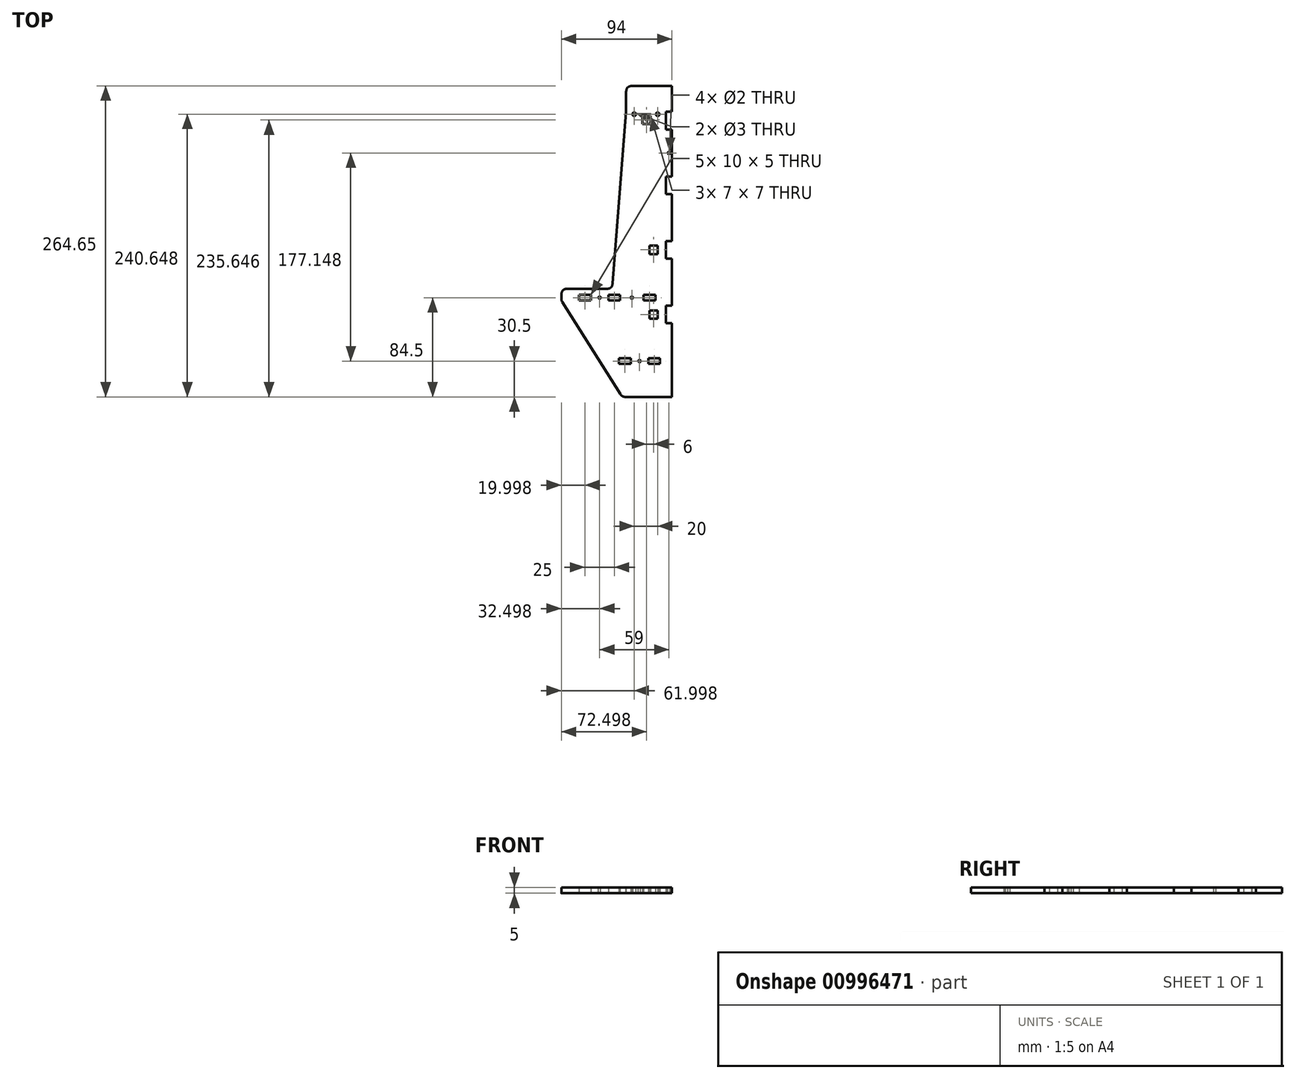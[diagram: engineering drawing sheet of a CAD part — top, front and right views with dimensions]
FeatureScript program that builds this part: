
annotation { "Feature Type Name" : "Feature", "Feature Type Description" : "" }
export const myFeature = defineFeature(function(context is Context, id is Id, definition is map)
    precondition{}
    {
        {
            var Q0;
            Q0=qCreatedBy(makeId("Top.planeOp"),FACE);
            var sketch = newSketch(context, id + "F0", { "sketchPlane" : qUnion([Q0])});
            skLineSegment(sketch, "E0", {"start": v(-76.42, -54.81) * mm, "end": v(-76.42, -44.81) * mm});
            skLineSegment(sketch, "E1", {"start": v(-33.23, -44.81) * mm, "end": v(-21.3, 105.84) * mm});
            skLineSegment(sketch, "E2", {"start": v(-21.3, 105.84) * mm, "end": v(12.58, 105.84) * mm, "construction": true});
            skLineSegment(sketch, "E3", {"start": v(17.58, 90.84) * mm, "end": v(17.58, 50.84) * mm});
            skLineSegment(sketch, "E4", {"start": v(17.58, -136.81) * mm, "end": v(-24.72, -136.81) * mm});
            skLineSegment(sketch, "E5", {"start": v(-24.72, -136.81) * mm, "end": v(-76.42, -54.81) * mm});
            skLineSegment(sketch, "E6.bottom", {"start": v(17.58, -74.16) * mm, "end": v(12.58, -74.16) * mm});
            skLineSegment(sketch, "E6.top", {"start": v(17.58, -59.16) * mm, "end": v(12.58, -59.16) * mm});
            skLineSegment(sketch, "E6.right", {"start": v(12.58, -74.16) * mm, "end": v(12.58, -59.16) * mm});
            skLineSegment(sketch, "E7.bottom", {"start": v(17.58, -19.16) * mm, "end": v(12.58, -19.16) * mm});
            skLineSegment(sketch, "E7.top", {"start": v(17.58, -4.16) * mm, "end": v(12.58, -4.16) * mm});
            skLineSegment(sketch, "E7.right", {"start": v(12.58, -19.16) * mm, "end": v(12.58, -4.16) * mm});
            skLineSegment(sketch, "E8.bottom", {"start": v(17.58, 35.84) * mm, "end": v(12.58, 35.84) * mm});
            skLineSegment(sketch, "E8.top", {"start": v(17.58, 50.84) * mm, "end": v(12.58, 50.84) * mm});
            skLineSegment(sketch, "E8.right", {"start": v(12.58, 35.84) * mm, "end": v(12.58, 50.84) * mm});
            skLineSegment(sketch, "E9.bottom", {"start": v(17.58, 90.84) * mm, "end": v(12.58, 90.84) * mm});
            skLineSegment(sketch, "E9.right", {"start": v(12.58, 90.84) * mm, "end": v(12.58, 105.84) * mm});
            skLineSegment(sketch, "E10.trimOffspring", {"start": v(17.58, 35.84) * mm, "end": v(17.58, -4.16) * mm});
            skLineSegment(sketch, "E11.trimOffspring", {"start": v(17.58, -19.16) * mm, "end": v(17.58, -59.16) * mm});
            skLineSegment(sketch, "E12.trimOffspring", {"start": v(17.58, -74.16) * mm, "end": v(17.58, -136.81) * mm});
            skPoint(sketch, "E13", {"position": v(17.58, -108.81) * mm});
            skLineSegment(sketch, "E14", {"start": v(17.58, -108.81) * mm, "end": v(-42.38, -108.81) * mm, "construction": true});
            skLineSegment(sketch, "E15.bottom", {"start": v(-2.42, -108.81) * mm, "end": v(7.58, -108.81) * mm});
            skLineSegment(sketch, "E15.top", {"start": v(-2.42, -103.81) * mm, "end": v(7.58, -103.81) * mm});
            skLineSegment(sketch, "E15.left", {"start": v(-2.42, -108.81) * mm, "end": v(-2.42, -103.81) * mm});
            skLineSegment(sketch, "E15.right", {"start": v(7.58, -108.81) * mm, "end": v(7.58, -103.81) * mm});
            skLineSegment(sketch, "E16.bottom", {"start": v(-27.42, -108.81) * mm, "end": v(-17.42, -108.81) * mm});
            skLineSegment(sketch, "E16.top", {"start": v(-27.42, -103.81) * mm, "end": v(-17.42, -103.81) * mm});
            skLineSegment(sketch, "E16.left", {"start": v(-27.42, -108.81) * mm, "end": v(-27.42, -103.81) * mm});
            skLineSegment(sketch, "E16.right", {"start": v(-17.42, -108.81) * mm, "end": v(-17.42, -103.81) * mm});
            skLineSegment(sketch, "E17", {"start": v(-76.42, -54.81) * mm, "end": v(17.58, -54.81) * mm, "construction": true});
            skLineSegment(sketch, "E18.bottom", {"start": v(-61.42, -54.81) * mm, "end": v(-51.42, -54.81) * mm});
            skLineSegment(sketch, "E18.top", {"start": v(-61.42, -49.81) * mm, "end": v(-51.42, -49.81) * mm});
            skLineSegment(sketch, "E18.left", {"start": v(-61.42, -54.81) * mm, "end": v(-61.42, -49.81) * mm});
            skLineSegment(sketch, "E18.right", {"start": v(-51.42, -54.81) * mm, "end": v(-51.42, -49.81) * mm});
            skLineSegment(sketch, "E19.bottom", {"start": v(-36.42, -54.81) * mm, "end": v(-26.42, -54.81) * mm});
            skLineSegment(sketch, "E19.top", {"start": v(-36.42, -49.81) * mm, "end": v(-26.42, -49.81) * mm});
            skLineSegment(sketch, "E19.left", {"start": v(-36.42, -54.81) * mm, "end": v(-36.42, -49.81) * mm});
            skLineSegment(sketch, "E19.right", {"start": v(-26.42, -54.81) * mm, "end": v(-26.42, -49.81) * mm});
            skLineSegment(sketch, "E20.bottom", {"start": v(-6.42, -54.81) * mm, "end": v(3.58, -54.81) * mm});
            skLineSegment(sketch, "E20.top", {"start": v(-6.42, -49.81) * mm, "end": v(3.58, -49.81) * mm});
            skLineSegment(sketch, "E20.left", {"start": v(-6.42, -54.81) * mm, "end": v(-6.42, -49.81) * mm});
            skLineSegment(sketch, "E20.right", {"start": v(3.58, -54.81) * mm, "end": v(3.58, -49.81) * mm});
            skPoint(sketch, "E21", {"position": v(-76.42, -44.81) * mm});
            skLineSegment(sketch, "E22", {"start": v(-33.23, -44.81) * mm, "end": v(17.58, -44.81) * mm, "construction": true});
            skLineSegment(sketch, "E23", {"start": v(-76.42, -44.81) * mm, "end": v(-33.23, -44.81) * mm});
            skLineSegment(sketch, "E24", {"start": v(-21.3, 105.84) * mm, "end": v(-21.3, 127.84) * mm});
            skLineSegment(sketch, "E25", {"start": v(-21.3, 127.84) * mm, "end": v(17.58, 127.84) * mm});
            skLineSegment(sketch, "E26", {"start": v(17.58, 127.84) * mm, "end": v(17.58, 105.84) * mm});
            skLineSegment(sketch, "E27", {"start": v(17.58, 105.84) * mm, "end": v(12.58, 105.84) * mm});
            skLineSegment(sketch, "E28.bottom", {"start": v(-7.42, 102.34) * mm, "end": v(-0.42, 102.34) * mm});
            skLineSegment(sketch, "E28.top", {"start": v(-7.42, 95.34) * mm, "end": v(-0.42, 95.34) * mm});
            skLineSegment(sketch, "E28.left", {"start": v(-7.42, 102.34) * mm, "end": v(-7.42, 95.34) * mm});
            skLineSegment(sketch, "E28.right", {"start": v(-0.42, 102.34) * mm, "end": v(-0.42, 95.34) * mm});
            skLineSegment(sketch, "E29.bottom", {"start": v(-1.42, -8.16) * mm, "end": v(5.58, -8.16) * mm});
            skLineSegment(sketch, "E29.top", {"start": v(-1.42, -15.16) * mm, "end": v(5.58, -15.16) * mm});
            skLineSegment(sketch, "E29.left", {"start": v(-1.42, -8.16) * mm, "end": v(-1.42, -15.16) * mm});
            skLineSegment(sketch, "E29.right", {"start": v(5.58, -8.16) * mm, "end": v(5.58, -15.16) * mm});
            skLineSegment(sketch, "E30.bottom", {"start": v(-1.42, -63.16) * mm, "end": v(5.58, -63.16) * mm});
            skLineSegment(sketch, "E30.top", {"start": v(-1.42, -70.16) * mm, "end": v(5.58, -70.16) * mm});
            skLineSegment(sketch, "E30.left", {"start": v(-1.42, -63.16) * mm, "end": v(-1.42, -70.16) * mm});
            skLineSegment(sketch, "E30.right", {"start": v(5.58, -63.16) * mm, "end": v(5.58, -70.16) * mm});
            skPoint(sketch, "E31", {"position": v(5.58, -11.66) * mm});
            skPoint(sketch, "E32", {"position": v(12.58, -11.66) * mm});
            skPoint(sketch, "E33", {"position": v(5.58, -66.66) * mm});
            skPoint(sketch, "E34", {"position": v(12.58, -66.66) * mm});
            skSolve(sketch);
        }
        {
            var Q0;
            Q0=makeQuery(id+"F0.imprint","IMPRINT",FACE,{"disambiguationData":[TD([[makeQuery(id+"F0.imprint","IMPRINT",EDGE,{"derivedFrom":sQuery(id+"F0.wireOp",EDGE,"E0")}),-1.0]])]});
            extrude(context, id + "F1", {"entities" : qUnion([Q0]), "depth" : 5 * mm, "offsetDistance" : 25 * mm});
        }
        {
            var Q0;
            Q0=makeQuery(id+"F1.opExtrude","SWEPT_EDGE",EDGE,{"disambiguationData":[OSD([sQuery(id+"F0.wireOp",EDGE,"E4"),sQuery(id+"F0.wireOp",EDGE,"E5")])]});
            var Q1;
            Q1=makeQuery(id+"F1.opExtrude","SWEPT_EDGE",EDGE,{"disambiguationData":[OSD([sQuery(id+"F0.wireOp",EDGE,"E4"),sQuery(id+"F0.wireOp",EDGE,"E5")])]});
            var Q2;
            Q2=makeQuery(id+"F1.opExtrude","SWEPT_EDGE",EDGE,{"disambiguationData":[OSD([sQuery(id+"F0.wireOp",EDGE,"E1"),sQuery(id+"F0.wireOp",EDGE,"E23")])]});
            var Q3;
            Q3=makeQuery(id+"F1.opExtrude","SWEPT_EDGE",EDGE,{"disambiguationData":[OSD([sQuery(id+"F0.wireOp",EDGE,"E0"),sQuery(id+"F0.wireOp",EDGE,"E5")])]});
            var Q4;
            Q4=makeQuery(id+"F1.opExtrude","SWEPT_EDGE",EDGE,{"disambiguationData":[OSD([sQuery(id+"F0.wireOp",EDGE,"E0"),sQuery(id+"F0.wireOp",EDGE,"E23")])]});
            var Q5;
            Q5=makeQuery(id+"F1.opExtrude","SWEPT_EDGE",EDGE,{"disambiguationData":[OSD([sQuery(id+"F0.wireOp",EDGE,"E1"),sQuery(id+"F0.wireOp",EDGE,"E24")])]});
            var Q6;
            Q6=makeQuery(id+"F1.opExtrude","SWEPT_EDGE",EDGE,{"disambiguationData":[OSD([sQuery(id+"F0.wireOp",EDGE,"E24"),sQuery(id+"F0.wireOp",EDGE,"E25")])]});
            fillet(context, id + "F2", {"entities" : qUnion([Q0, Q1, Q2, Q3, Q4, Q5, Q6]), "radius" : 5 * mm, "tangentPropagation" : true, "rho" : 0.5, "crossSection" : FilletCrossSection.CONIC, "allowEdgeOverflow" : false});
        }
        {
            var Q0;
            Q0=makeQuery(id+"F1.opExtrude","CAP_FACE",FACE,{"disambiguationData":[OSD([sQuery(id+"F0.wireOp",EDGE,"E0"),sQuery(id+"F0.wireOp",EDGE,"E1"),sQuery(id+"F0.wireOp",EDGE,"E3"),sQuery(id+"F0.wireOp",EDGE,"E4"),sQuery(id+"F0.wireOp",EDGE,"E5"),sQuery(id+"F0.wireOp",EDGE,"E6.bottom"),sQuery(id+"F0.wireOp",EDGE,"E6.top"),sQuery(id+"F0.wireOp",EDGE,"E6.right"),sQuery(id+"F0.wireOp",EDGE,"E7.bottom"),sQuery(id+"F0.wireOp",EDGE,"E7.top"),sQuery(id+"F0.wireOp",EDGE,"E7.right"),sQuery(id+"F0.wireOp",EDGE,"E8.bottom"),sQuery(id+"F0.wireOp",EDGE,"E8.top"),sQuery(id+"F0.wireOp",EDGE,"E8.right"),sQuery(id+"F0.wireOp",EDGE,"E9.bottom"),sQuery(id+"F0.wireOp",EDGE,"E9.right"),sQuery(id+"F0.wireOp",EDGE,"E10.trimOffspring"),sQuery(id+"F0.wireOp",EDGE,"E11.trimOffspring"),sQuery(id+"F0.wireOp",EDGE,"E12.trimOffspring"),sQuery(id+"F0.wireOp",EDGE,"E15.bottom"),sQuery(id+"F0.wireOp",EDGE,"E15.top"),sQuery(id+"F0.wireOp",EDGE,"E15.left"),sQuery(id+"F0.wireOp",EDGE,"E15.right"),sQuery(id+"F0.wireOp",EDGE,"E16.bottom"),sQuery(id+"F0.wireOp",EDGE,"E16.top"),sQuery(id+"F0.wireOp",EDGE,"E16.left"),sQuery(id+"F0.wireOp",EDGE,"E16.right"),sQuery(id+"F0.wireOp",EDGE,"E18.bottom"),sQuery(id+"F0.wireOp",EDGE,"E18.top"),sQuery(id+"F0.wireOp",EDGE,"E18.left"),sQuery(id+"F0.wireOp",EDGE,"E18.right"),sQuery(id+"F0.wireOp",EDGE,"E19.bottom"),sQuery(id+"F0.wireOp",EDGE,"E19.top"),sQuery(id+"F0.wireOp",EDGE,"E19.left"),sQuery(id+"F0.wireOp",EDGE,"E19.right"),sQuery(id+"F0.wireOp",EDGE,"E20.bottom"),sQuery(id+"F0.wireOp",EDGE,"E20.top"),sQuery(id+"F0.wireOp",EDGE,"E20.left"),sQuery(id+"F0.wireOp",EDGE,"E20.right"),sQuery(id+"F0.wireOp",EDGE,"E23"),sQuery(id+"F0.wireOp",EDGE,"E24"),sQuery(id+"F0.wireOp",EDGE,"E25"),sQuery(id+"F0.wireOp",EDGE,"E26"),sQuery(id+"F0.wireOp",EDGE,"E27")])],"isStart":false});
            var sketch = newSketch(context, id + "F3", { "sketchPlane" : qUnion([Q0])});
            skPoint(sketch, "E35", {"position": v(-14.42, 103.84) * mm});
            skPoint(sketch, "E36", {"position": v(5.58, 103.84) * mm});
            skSolve(sketch);
        }
        {
            var Q0;
            Q0=sQuery(id+"F3.wireOp",VERTEX,"E36");
            var Q1;
            Q1=sQuery(id+"F3.wireOp",VERTEX,"E35");
            var Q2;
            Q2=makeQuery(id+"F1.opExtrude","SWEPT_BODY",BODY,{"disambiguationData":[OSD([sQuery(id+"F0.wireOp",EDGE,"E0"),sQuery(id+"F0.wireOp",EDGE,"E1"),sQuery(id+"F0.wireOp",EDGE,"E3"),sQuery(id+"F0.wireOp",EDGE,"E4"),sQuery(id+"F0.wireOp",EDGE,"E5"),sQuery(id+"F0.wireOp",EDGE,"E6.bottom"),sQuery(id+"F0.wireOp",EDGE,"E6.top"),sQuery(id+"F0.wireOp",EDGE,"E6.right"),sQuery(id+"F0.wireOp",EDGE,"E7.bottom"),sQuery(id+"F0.wireOp",EDGE,"E7.top"),sQuery(id+"F0.wireOp",EDGE,"E7.right"),sQuery(id+"F0.wireOp",EDGE,"E8.bottom"),sQuery(id+"F0.wireOp",EDGE,"E8.top"),sQuery(id+"F0.wireOp",EDGE,"E8.right"),sQuery(id+"F0.wireOp",EDGE,"E9.bottom"),sQuery(id+"F0.wireOp",EDGE,"E9.right"),sQuery(id+"F0.wireOp",EDGE,"E10.trimOffspring"),sQuery(id+"F0.wireOp",EDGE,"E11.trimOffspring"),sQuery(id+"F0.wireOp",EDGE,"E12.trimOffspring"),sQuery(id+"F0.wireOp",EDGE,"E15.bottom"),sQuery(id+"F0.wireOp",EDGE,"E15.top"),sQuery(id+"F0.wireOp",EDGE,"E15.left"),sQuery(id+"F0.wireOp",EDGE,"E15.right"),sQuery(id+"F0.wireOp",EDGE,"E16.bottom"),sQuery(id+"F0.wireOp",EDGE,"E16.top"),sQuery(id+"F0.wireOp",EDGE,"E16.left"),sQuery(id+"F0.wireOp",EDGE,"E16.right"),sQuery(id+"F0.wireOp",EDGE,"E18.bottom"),sQuery(id+"F0.wireOp",EDGE,"E18.top"),sQuery(id+"F0.wireOp",EDGE,"E18.left"),sQuery(id+"F0.wireOp",EDGE,"E18.right"),sQuery(id+"F0.wireOp",EDGE,"E19.bottom"),sQuery(id+"F0.wireOp",EDGE,"E19.top"),sQuery(id+"F0.wireOp",EDGE,"E19.left"),sQuery(id+"F0.wireOp",EDGE,"E19.right"),sQuery(id+"F0.wireOp",EDGE,"E20.bottom"),sQuery(id+"F0.wireOp",EDGE,"E20.top"),sQuery(id+"F0.wireOp",EDGE,"E20.left"),sQuery(id+"F0.wireOp",EDGE,"E20.right"),sQuery(id+"F0.wireOp",EDGE,"E23"),sQuery(id+"F0.wireOp",EDGE,"E24"),sQuery(id+"F0.wireOp",EDGE,"E25"),sQuery(id+"F0.wireOp",EDGE,"E26"),sQuery(id+"F0.wireOp",EDGE,"E27")])]});
            hole(context, id + "F4", {"style" : HoleStyle.SIMPLE, "endStyle" : HoleEndStyle.THROUGH, "holeDiameter" : 3 * mm, "majorDiameter" : 5 * mm, "isTappedThrough" : true, "tappedDepth" : 12 * mm, "tapClearance" : 3, "locations" : qUnion([Q0, Q1]), "scope" : qUnion([Q2])});
        }
        {
            var Q0;
            Q0=makeQuery(id+"F1.opExtrude","CAP_FACE",FACE,{"disambiguationData":[OSD([sQuery(id+"F0.wireOp",EDGE,"E0"),sQuery(id+"F0.wireOp",EDGE,"E1"),sQuery(id+"F0.wireOp",EDGE,"E3"),sQuery(id+"F0.wireOp",EDGE,"E4"),sQuery(id+"F0.wireOp",EDGE,"E5"),sQuery(id+"F0.wireOp",EDGE,"E6.bottom"),sQuery(id+"F0.wireOp",EDGE,"E6.top"),sQuery(id+"F0.wireOp",EDGE,"E6.right"),sQuery(id+"F0.wireOp",EDGE,"E7.bottom"),sQuery(id+"F0.wireOp",EDGE,"E7.top"),sQuery(id+"F0.wireOp",EDGE,"E7.right"),sQuery(id+"F0.wireOp",EDGE,"E8.bottom"),sQuery(id+"F0.wireOp",EDGE,"E8.top"),sQuery(id+"F0.wireOp",EDGE,"E8.right"),sQuery(id+"F0.wireOp",EDGE,"E9.bottom"),sQuery(id+"F0.wireOp",EDGE,"E9.right"),sQuery(id+"F0.wireOp",EDGE,"E10.trimOffspring"),sQuery(id+"F0.wireOp",EDGE,"E11.trimOffspring"),sQuery(id+"F0.wireOp",EDGE,"E12.trimOffspring"),sQuery(id+"F0.wireOp",EDGE,"E15.bottom"),sQuery(id+"F0.wireOp",EDGE,"E15.top"),sQuery(id+"F0.wireOp",EDGE,"E15.left"),sQuery(id+"F0.wireOp",EDGE,"E15.right"),sQuery(id+"F0.wireOp",EDGE,"E16.bottom"),sQuery(id+"F0.wireOp",EDGE,"E16.top"),sQuery(id+"F0.wireOp",EDGE,"E16.left"),sQuery(id+"F0.wireOp",EDGE,"E16.right"),sQuery(id+"F0.wireOp",EDGE,"E18.bottom"),sQuery(id+"F0.wireOp",EDGE,"E18.top"),sQuery(id+"F0.wireOp",EDGE,"E18.left"),sQuery(id+"F0.wireOp",EDGE,"E18.right"),sQuery(id+"F0.wireOp",EDGE,"E19.bottom"),sQuery(id+"F0.wireOp",EDGE,"E19.top"),sQuery(id+"F0.wireOp",EDGE,"E19.left"),sQuery(id+"F0.wireOp",EDGE,"E19.right"),sQuery(id+"F0.wireOp",EDGE,"E20.bottom"),sQuery(id+"F0.wireOp",EDGE,"E20.top"),sQuery(id+"F0.wireOp",EDGE,"E20.left"),sQuery(id+"F0.wireOp",EDGE,"E20.right"),sQuery(id+"F0.wireOp",EDGE,"E23"),sQuery(id+"F0.wireOp",EDGE,"E24"),sQuery(id+"F0.wireOp",EDGE,"E25"),sQuery(id+"F0.wireOp",EDGE,"E26"),sQuery(id+"F0.wireOp",EDGE,"E27")])],"isStart":false});
            var sketch = newSketch(context, id + "F5", { "sketchPlane" : qUnion([Q0])});
            skLineSegment(sketch, "E37", {"start": v(-51.42, -52.31) * mm, "end": v(-36.42, -52.31) * mm, "construction": true});
            skLineSegment(sketch, "E38", {"start": v(-26.42, -52.31) * mm, "end": v(-6.42, -52.31) * mm, "construction": true});
            skPoint(sketch, "E39", {"position": v(-43.92, -52.31) * mm});
            skPoint(sketch, "E40", {"position": v(-16.42, -52.31) * mm});
            skLineSegment(sketch, "E41", {"start": v(-17.42, -106.31) * mm, "end": v(-2.42, -106.31) * mm, "construction": true});
            skPoint(sketch, "E42", {"position": v(-9.92, -106.31) * mm});
            skPoint(sketch, "E43", {"position": v(15.08, 70.84) * mm});
            skPoint(sketch, "E43.positionSnap0", {"position": v(17.58, 70.84) * mm});
            skSolve(sketch);
        }
        {
            var Q0;
            Q0=sQuery(id+"F5.wireOp",VERTEX,"E39");
            var Q1;
            Q1=sQuery(id+"F5.wireOp",VERTEX,"E40");
            var Q2;
            Q2=sQuery(id+"F5.wireOp",VERTEX,"E42");
            var Q3;
            Q3=sQuery(id+"F5.wireOp",VERTEX,"E43");
            var Q4;
            Q4=makeQuery(id+"F1.opExtrude","SWEPT_BODY",BODY,{"disambiguationData":[OSD([sQuery(id+"F0.wireOp",EDGE,"E0"),sQuery(id+"F0.wireOp",EDGE,"E1"),sQuery(id+"F0.wireOp",EDGE,"E3"),sQuery(id+"F0.wireOp",EDGE,"E4"),sQuery(id+"F0.wireOp",EDGE,"E5"),sQuery(id+"F0.wireOp",EDGE,"E6.bottom"),sQuery(id+"F0.wireOp",EDGE,"E6.top"),sQuery(id+"F0.wireOp",EDGE,"E6.right"),sQuery(id+"F0.wireOp",EDGE,"E7.bottom"),sQuery(id+"F0.wireOp",EDGE,"E7.top"),sQuery(id+"F0.wireOp",EDGE,"E7.right"),sQuery(id+"F0.wireOp",EDGE,"E8.bottom"),sQuery(id+"F0.wireOp",EDGE,"E8.top"),sQuery(id+"F0.wireOp",EDGE,"E8.right"),sQuery(id+"F0.wireOp",EDGE,"E9.bottom"),sQuery(id+"F0.wireOp",EDGE,"E9.right"),sQuery(id+"F0.wireOp",EDGE,"E10.trimOffspring"),sQuery(id+"F0.wireOp",EDGE,"E11.trimOffspring"),sQuery(id+"F0.wireOp",EDGE,"E12.trimOffspring"),sQuery(id+"F0.wireOp",EDGE,"E15.bottom"),sQuery(id+"F0.wireOp",EDGE,"E15.top"),sQuery(id+"F0.wireOp",EDGE,"E15.left"),sQuery(id+"F0.wireOp",EDGE,"E15.right"),sQuery(id+"F0.wireOp",EDGE,"E16.bottom"),sQuery(id+"F0.wireOp",EDGE,"E16.top"),sQuery(id+"F0.wireOp",EDGE,"E16.left"),sQuery(id+"F0.wireOp",EDGE,"E16.right"),sQuery(id+"F0.wireOp",EDGE,"E18.bottom"),sQuery(id+"F0.wireOp",EDGE,"E18.top"),sQuery(id+"F0.wireOp",EDGE,"E18.left"),sQuery(id+"F0.wireOp",EDGE,"E18.right"),sQuery(id+"F0.wireOp",EDGE,"E19.bottom"),sQuery(id+"F0.wireOp",EDGE,"E19.top"),sQuery(id+"F0.wireOp",EDGE,"E19.left"),sQuery(id+"F0.wireOp",EDGE,"E19.right"),sQuery(id+"F0.wireOp",EDGE,"E20.bottom"),sQuery(id+"F0.wireOp",EDGE,"E20.top"),sQuery(id+"F0.wireOp",EDGE,"E20.left"),sQuery(id+"F0.wireOp",EDGE,"E20.right"),sQuery(id+"F0.wireOp",EDGE,"E23"),sQuery(id+"F0.wireOp",EDGE,"E24"),sQuery(id+"F0.wireOp",EDGE,"E25"),sQuery(id+"F0.wireOp",EDGE,"E26"),sQuery(id+"F0.wireOp",EDGE,"E27")])]});
            hole(context, id + "F6", {"style" : HoleStyle.SIMPLE, "endStyle" : HoleEndStyle.THROUGH, "holeDiameter" : 2 * mm, "majorDiameter" : 5 * mm, "isTappedThrough" : true, "tappedDepth" : 12 * mm, "tapClearance" : 3, "locations" : qUnion([Q0, Q1, Q2, Q3]), "scope" : qUnion([Q4])});
        }
    });
